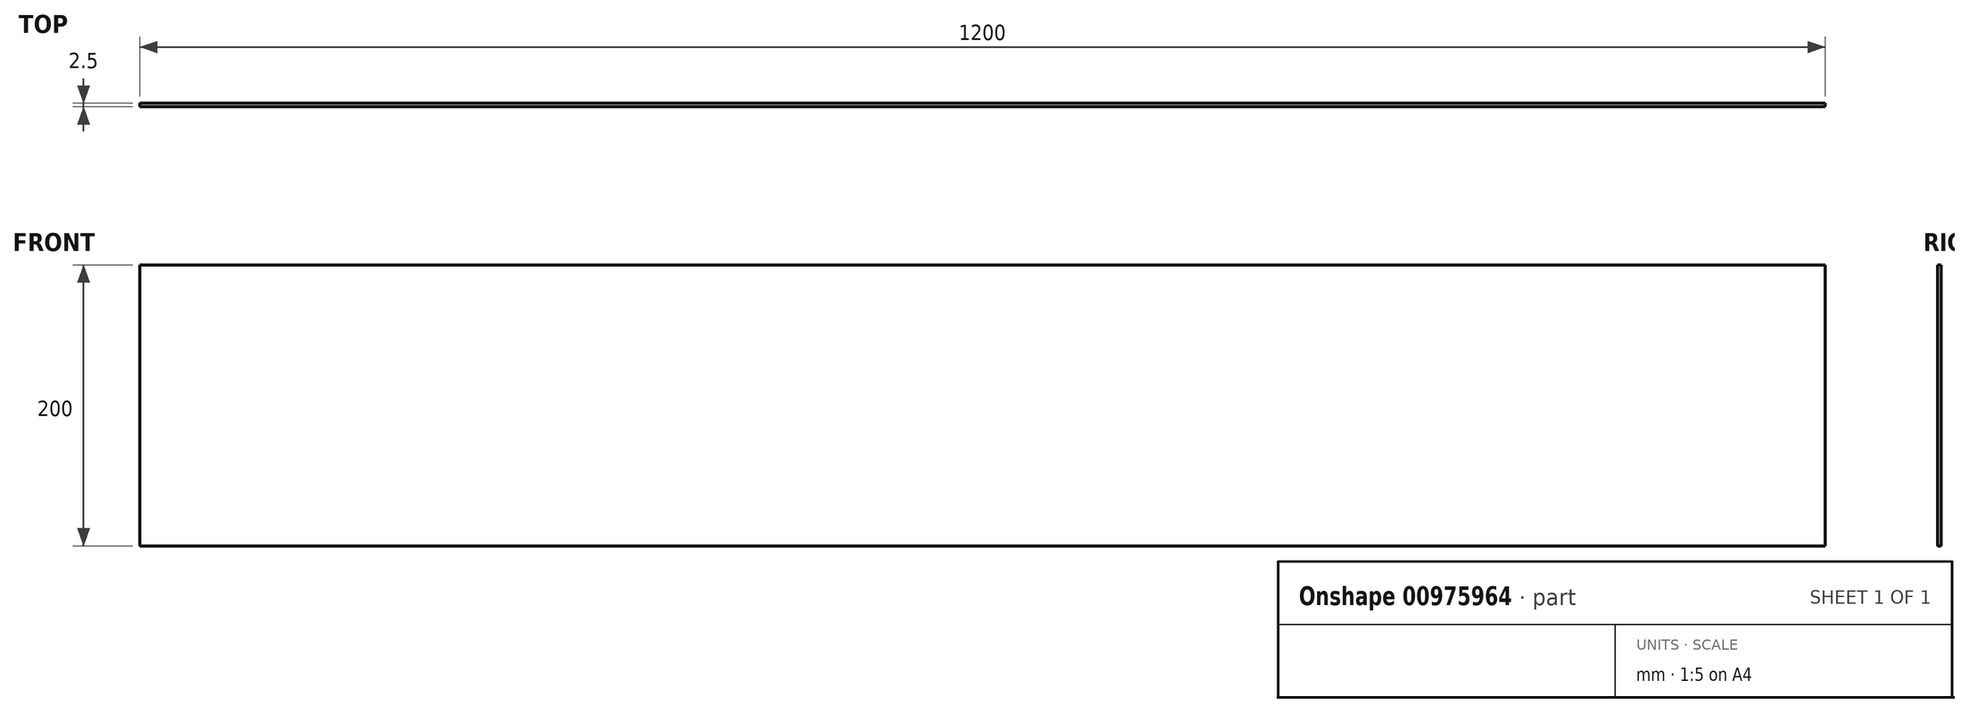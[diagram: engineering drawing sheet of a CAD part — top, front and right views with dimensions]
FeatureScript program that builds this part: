
annotation { "Feature Type Name" : "Feature", "Feature Type Description" : "" }
export const myFeature = defineFeature(function(context is Context, id is Id, definition is map)
    precondition{}
    {
        {
            var Q0;
            Q0=qCreatedBy(makeId("Front.planeOp"),FACE);
            var sketch = newSketch(context, id + "F0", { "sketchPlane" : qUnion([Q0])});
            skLineSegment(sketch, "E0.bottom", {"start": v(600, -100) * mm, "end": v(-600, -100) * mm});
            skLineSegment(sketch, "E0.top", {"start": v(600, 100) * mm, "end": v(-600, 100) * mm});
            skLineSegment(sketch, "E0.left", {"start": v(600, -100) * mm, "end": v(600, 100) * mm});
            skLineSegment(sketch, "E0.right", {"start": v(-600, -100) * mm, "end": v(-600, 100) * mm});
            skPoint(sketch, "E0.middle", {"position": v(0, 0) * mm});
            skSolve(sketch);
        }
        {
            var Q0;
            Q0 = qSketchRegion(id + "F0", true);
            extrude(context, id + "F1", {"entities" : qUnion([Q0]), "endBound" : BoundingType.SYMMETRIC, "depth" : 2.5 * mm, "offsetDistance" : 25 * mm});
        }
    });
